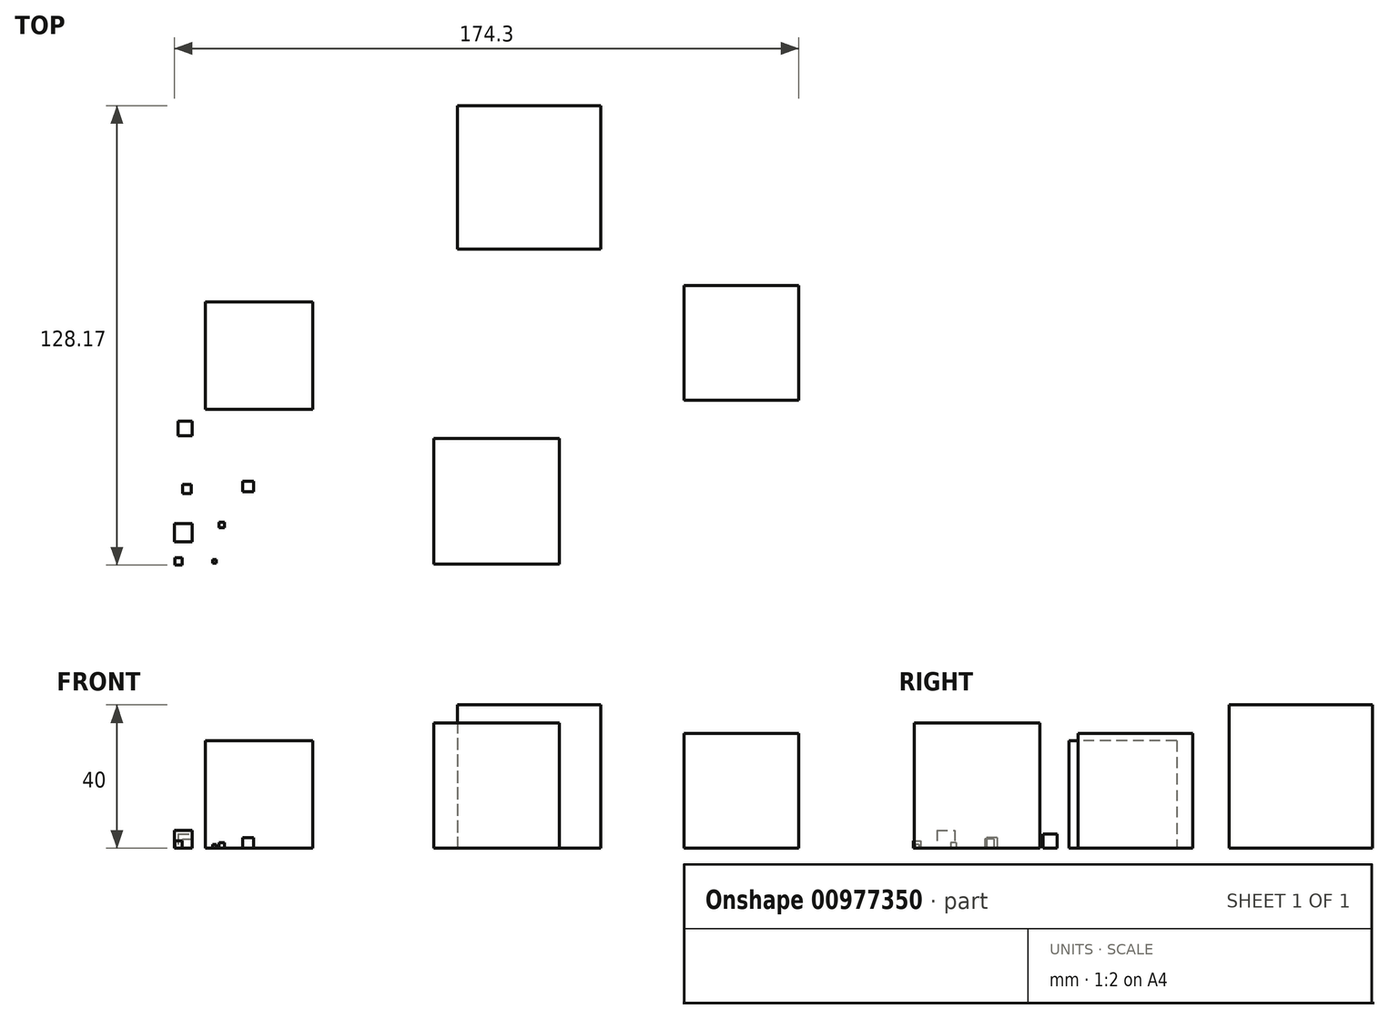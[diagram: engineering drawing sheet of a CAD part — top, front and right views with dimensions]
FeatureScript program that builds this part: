
annotation { "Feature Type Name" : "Feature", "Feature Type Description" : "" }
export const myFeature = defineFeature(function(context is Context, id is Id, definition is map)
    precondition{}
    {
        {
            var Q0;
            Q0=qCreatedBy(makeId("Top.planeOp"),FACE);
            var sketch = newSketch(context, id + "F0", { "sketchPlane" : qUnion([Q0])});
            skLineSegment(sketch, "E0.bottom", {"start": v(-70.26, -69.47) * mm, "end": v(-72.26, -69.47) * mm});
            skLineSegment(sketch, "E0.top", {"start": v(-70.26, -67.47) * mm, "end": v(-72.26, -67.47) * mm});
            skLineSegment(sketch, "E0.left", {"start": v(-70.26, -69.47) * mm, "end": v(-70.26, -67.47) * mm});
            skLineSegment(sketch, "E0.right", {"start": v(-72.26, -69.47) * mm, "end": v(-72.26, -67.47) * mm});
            skSolve(sketch);
        }
        {
            var Q0;
            Q0=qCreatedBy(makeId("Top.planeOp"),FACE);
            var sketch = newSketch(context, id + "F1", { "sketchPlane" : qUnion([Q0])});
            skLineSegment(sketch, "E1.bottom", {"start": v(-67.48, -62.92) * mm, "end": v(-72.48, -62.92) * mm});
            skLineSegment(sketch, "E1.top", {"start": v(-67.48, -57.92) * mm, "end": v(-72.48, -57.92) * mm});
            skLineSegment(sketch, "E1.left", {"start": v(-67.48, -62.92) * mm, "end": v(-67.48, -57.92) * mm});
            skLineSegment(sketch, "E1.right", {"start": v(-72.48, -62.92) * mm, "end": v(-72.48, -57.92) * mm});
            skSolve(sketch);
        }
        {
            var Q0;
            Q0=makeQuery(id+"F0.imprint","IMPRINT",FACE,{"disambiguationData":[TD([[makeQuery(id+"F0.imprint","IMPRINT",EDGE,{"derivedFrom":sQuery(id+"F0.wireOp",EDGE,"E0.bottom")}),-1.0]])]});
            extrude(context, id + "F2", {"entities" : qUnion([Q0]), "depth" : 2 * mm, "offsetDistance" : 25 * mm});
        }
        {
            var Q0;
            Q0=makeQuery(id+"F1.imprint","IMPRINT",FACE,{"disambiguationData":[TD([[makeQuery(id+"F1.imprint","IMPRINT",EDGE,{"derivedFrom":sQuery(id+"F1.wireOp",EDGE,"E1.bottom")}),-1.0]])]});
            extrude(context, id + "F3", {"entities" : qUnion([Q0]), "depth" : 5 * mm, "offsetDistance" : 25 * mm});
        }
        {
            var Q0;
            Q0=qCreatedBy(makeId("Top.planeOp"),FACE);
            var sketch = newSketch(context, id + "F4", { "sketchPlane" : qUnion([Q0])});
            skLineSegment(sketch, "E2.bottom", {"start": v(-61.75, -67.93) * mm, "end": v(-60.75, -67.93) * mm});
            skLineSegment(sketch, "E2.top", {"start": v(-61.75, -68.93) * mm, "end": v(-60.75, -68.93) * mm});
            skLineSegment(sketch, "E2.left", {"start": v(-61.75, -67.93) * mm, "end": v(-61.75, -68.93) * mm});
            skLineSegment(sketch, "E2.right", {"start": v(-60.75, -67.93) * mm, "end": v(-60.75, -68.93) * mm});
            skSolve(sketch);
        }
        {
            var Q0;
            Q0=qCreatedBy(makeId("Top.planeOp"),FACE);
            var sketch = newSketch(context, id + "F5", { "sketchPlane" : qUnion([Q0])});
            skLineSegment(sketch, "E3.bottom", {"start": v(-59.94, -57.57) * mm, "end": v(-58.44, -57.57) * mm});
            skLineSegment(sketch, "E3.top", {"start": v(-59.94, -59.07) * mm, "end": v(-58.44, -59.07) * mm});
            skLineSegment(sketch, "E3.left", {"start": v(-59.94, -57.57) * mm, "end": v(-59.94, -59.07) * mm});
            skLineSegment(sketch, "E3.right", {"start": v(-58.44, -57.57) * mm, "end": v(-58.44, -59.07) * mm});
            skSolve(sketch);
        }
        {
            var Q0;
            Q0=qCreatedBy(makeId("Top.planeOp"),FACE);
            var sketch = newSketch(context, id + "F6", { "sketchPlane" : qUnion([Q0])});
            skLineSegment(sketch, "E4.bottom", {"start": v(-70.2, -46.99) * mm, "end": v(-67.7, -46.99) * mm});
            skLineSegment(sketch, "E4.top", {"start": v(-70.2, -49.49) * mm, "end": v(-67.7, -49.49) * mm});
            skLineSegment(sketch, "E4.left", {"start": v(-70.2, -46.99) * mm, "end": v(-70.2, -49.49) * mm});
            skLineSegment(sketch, "E4.right", {"start": v(-67.7, -46.99) * mm, "end": v(-67.7, -49.49) * mm});
            skSolve(sketch);
        }
        {
            var Q0;
            Q0=qCreatedBy(makeId("Top.planeOp"),FACE);
            var sketch = newSketch(context, id + "F7", { "sketchPlane" : qUnion([Q0])});
            skLineSegment(sketch, "E5.bottom", {"start": v(-53.36, -46.07) * mm, "end": v(-50.36, -46.07) * mm});
            skLineSegment(sketch, "E5.top", {"start": v(-53.36, -49.07) * mm, "end": v(-50.36, -49.07) * mm});
            skLineSegment(sketch, "E5.left", {"start": v(-53.36, -46.07) * mm, "end": v(-53.36, -49.07) * mm});
            skLineSegment(sketch, "E5.right", {"start": v(-50.36, -46.07) * mm, "end": v(-50.36, -49.07) * mm});
            skSolve(sketch);
        }
        {
            var Q0;
            Q0=qCreatedBy(makeId("Top.planeOp"),FACE);
            var sketch = newSketch(context, id + "F8", { "sketchPlane" : qUnion([Q0])});
            skLineSegment(sketch, "E6.bottom", {"start": v(-71.44, -29.34) * mm, "end": v(-67.44, -29.34) * mm});
            skLineSegment(sketch, "E6.top", {"start": v(-71.44, -33.34) * mm, "end": v(-67.44, -33.34) * mm});
            skLineSegment(sketch, "E6.left", {"start": v(-71.44, -29.34) * mm, "end": v(-71.44, -33.34) * mm});
            skLineSegment(sketch, "E6.right", {"start": v(-67.44, -29.34) * mm, "end": v(-67.44, -33.34) * mm});
            skSolve(sketch);
        }
        {
            var Q0;
            Q0=makeQuery(id+"F6.imprint","IMPRINT",FACE,{"disambiguationData":[TD([[makeQuery(id+"F6.imprint","IMPRINT",EDGE,{"derivedFrom":sQuery(id+"F6.wireOp",EDGE,"E4.bottom")}),-1.0]])]});
            extrude(context, id + "F9", {"entities" : qUnion([Q0]), "depth" : 2.5 * mm, "offsetDistance" : 25 * mm});
        }
        {
            var Q0;
            Q0=makeQuery(id+"F8.imprint","IMPRINT",FACE,{"disambiguationData":[TD([[makeQuery(id+"F8.imprint","IMPRINT",EDGE,{"derivedFrom":sQuery(id+"F8.wireOp",EDGE,"E6.bottom")}),-1.0]])]});
            extrude(context, id + "F10", {"entities" : qUnion([Q0]), "depth" : 4 * mm, "offsetDistance" : 25 * mm});
        }
        {
            var Q0;
            Q0=makeQuery(id+"F7.imprint","IMPRINT",FACE,{"disambiguationData":[TD([[makeQuery(id+"F7.imprint","IMPRINT",EDGE,{"derivedFrom":sQuery(id+"F7.wireOp",EDGE,"E5.bottom")}),-1.0]])]});
            extrude(context, id + "F11", {"entities" : qUnion([Q0]), "depth" : 3 * mm, "offsetDistance" : 25 * mm});
        }
        {
            var Q0;
            Q0=makeQuery(id+"F5.imprint","IMPRINT",FACE,{"disambiguationData":[TD([[makeQuery(id+"F5.imprint","IMPRINT",EDGE,{"derivedFrom":sQuery(id+"F5.wireOp",EDGE,"E3.bottom")}),-1.0]])]});
            extrude(context, id + "F12", {"entities" : qUnion([Q0]), "depth" : 1.5 * mm, "offsetDistance" : 25 * mm});
        }
        {
            var Q0;
            Q0=makeQuery(id+"F4.imprint","IMPRINT",FACE,{"disambiguationData":[TD([[makeQuery(id+"F4.imprint","IMPRINT",EDGE,{"derivedFrom":sQuery(id+"F4.wireOp",EDGE,"E2.bottom")}),-1.0]])]});
            extrude(context, id + "F13", {"entities" : qUnion([Q0]), "depth" : 1 * mm, "offsetDistance" : 25 * mm});
        }
        {
            var Q0;
            Q0=qCreatedBy(makeId("Top.planeOp"),FACE);
            var sketch = newSketch(context, id + "F14", { "sketchPlane" : qUnion([Q0])});
            skLineSegment(sketch, "E7.bottom", {"start": v(-63.82, 4.01) * mm, "end": v(-33.82, 4.01) * mm});
            skLineSegment(sketch, "E7.top", {"start": v(-63.82, -25.99) * mm, "end": v(-33.82, -25.99) * mm});
            skLineSegment(sketch, "E7.left", {"start": v(-63.82, 4.01) * mm, "end": v(-63.82, -25.99) * mm});
            skLineSegment(sketch, "E7.right", {"start": v(-33.82, 4.01) * mm, "end": v(-33.82, -25.99) * mm});
            skSolve(sketch);
        }
        {
            var Q0;
            Q0=makeQuery(id+"F14.imprint","IMPRINT",FACE,{"disambiguationData":[TD([[makeQuery(id+"F14.imprint","IMPRINT",EDGE,{"derivedFrom":sQuery(id+"F14.wireOp",EDGE,"E7.bottom")}),-1.0]])]});
            extrude(context, id + "F15", {"entities" : qUnion([Q0]), "depth" : 30 * mm, "offsetDistance" : 25 * mm});
        }
        {
            var Q0;
            Q0=qCreatedBy(makeId("Top.planeOp"),FACE);
            var sketch = newSketch(context, id + "F16", { "sketchPlane" : qUnion([Q0])});
            skLineSegment(sketch, "E8.bottom", {"start": v(6.51, 58.7) * mm, "end": v(46.51, 58.7) * mm});
            skLineSegment(sketch, "E8.top", {"start": v(6.51, 18.7) * mm, "end": v(46.51, 18.7) * mm});
            skLineSegment(sketch, "E8.left", {"start": v(6.51, 58.7) * mm, "end": v(6.51, 18.7) * mm});
            skLineSegment(sketch, "E8.right", {"start": v(46.51, 58.7) * mm, "end": v(46.51, 18.7) * mm});
            skSolve(sketch);
        }
        {
            var Q0;
            Q0=makeQuery(id+"F16.imprint","IMPRINT",FACE,{"disambiguationData":[TD([[makeQuery(id+"F16.imprint","IMPRINT",EDGE,{"derivedFrom":sQuery(id+"F16.wireOp",EDGE,"E8.bottom")}),-1.0]])]});
            extrude(context, id + "F17", {"entities" : qUnion([Q0]), "depth" : 40 * mm, "offsetDistance" : 25 * mm});
        }
        {
            var Q0;
            Q0=qCreatedBy(makeId("Top.planeOp"),FACE);
            var sketch = newSketch(context, id + "F18", { "sketchPlane" : qUnion([Q0])});
            skLineSegment(sketch, "E9.bottom", {"start": v(0, -34.2) * mm, "end": v(35, -34.2) * mm});
            skLineSegment(sketch, "E9.top", {"start": v(0, -69.2) * mm, "end": v(35, -69.2) * mm});
            skLineSegment(sketch, "E9.left", {"start": v(0, -34.2) * mm, "end": v(0, -69.2) * mm});
            skLineSegment(sketch, "E9.right", {"start": v(35, -34.2) * mm, "end": v(35, -69.2) * mm});
            skSolve(sketch);
        }
        {
            var Q0;
            Q0=makeQuery(id+"F18.imprint","IMPRINT",FACE,{"disambiguationData":[TD([[makeQuery(id+"F18.imprint","IMPRINT",EDGE,{"derivedFrom":sQuery(id+"F18.wireOp",EDGE,"E9.bottom")}),-1.0]])]});
            extrude(context, id + "F19", {"entities" : qUnion([Q0]), "depth" : 35 * mm, "offsetDistance" : 25 * mm});
        }
        {
            var Q0;
            Q0=qCreatedBy(makeId("Top.planeOp"),FACE);
            var sketch = newSketch(context, id + "F20", { "sketchPlane" : qUnion([Q0])});
            skLineSegment(sketch, "E10.bottom", {"start": v(69.82, 8.51) * mm, "end": v(101.82, 8.51) * mm});
            skLineSegment(sketch, "E10.top", {"start": v(69.82, -23.49) * mm, "end": v(101.82, -23.49) * mm});
            skLineSegment(sketch, "E10.left", {"start": v(69.82, 8.51) * mm, "end": v(69.82, -23.49) * mm});
            skLineSegment(sketch, "E10.right", {"start": v(101.82, 8.51) * mm, "end": v(101.82, -23.49) * mm});
            skSolve(sketch);
        }
        {
            var Q0;
            Q0=makeQuery(id+"F20.imprint","IMPRINT",FACE,{"disambiguationData":[TD([[makeQuery(id+"F20.imprint","IMPRINT",EDGE,{"derivedFrom":sQuery(id+"F20.wireOp",EDGE,"E10.bottom")}),-1.0]])]});
            extrude(context, id + "F21", {"entities" : qUnion([Q0]), "depth" : 32 * mm, "offsetDistance" : 25 * mm});
        }
    });
